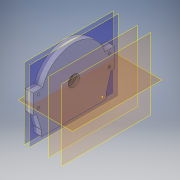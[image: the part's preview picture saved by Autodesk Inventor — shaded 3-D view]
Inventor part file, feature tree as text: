
AUTODESK INVENTOR PART (.ipt)
format: ipt  version: 2019 (Build 230136000, 136)  size: 506,368 bytes
history: native  units: mm
features: sketch x28, extrude x21, mirror x13, plane x12, projected_geometry x11, fillet x4, hole x3, other x2
ambient origin geometry x8: Origin, YZ Plane, XZ Plane, XY Plane, X Axis, Y Axis, Z Axis, Center Point
bodies: Body1 (feature_tree)
feature tree (94):
  other  "實體1"
  extrude  "擠出1"  Depth=123.43mm
  plane  "工作平面2"
  extrude  "擠出3"  Depth=160.0mm
  plane  "工作平面3"
  sketch  "草圖5"
  extrude  "擠出4"  Depth=120.0mm TaperAngle=0.0deg
  extrude  "擠出5"  [1 undecoded]
  plane  "工作平面4"
  extrude  "擠出7"  Depth=130.0mm
  plane  "工作平面5"
  extrude  "擠出9"  Depth=15.0mm TaperAngle=0.0deg
  extrude  "擠出10"  [1 undecoded]
  extrude  "擠出11"  Depth=140.0mm
  extrude  "擠出12"  Depth=10.0mm TaperAngle=0.0deg
  mirror  "鏡射1"
  fillet  "圓角2"  Radius=10.0mm
  fillet  "圓角3"  Radius=10.0mm
  sketch  "草圖16"
  plane  "工作平面7"
  mirror  "鏡射2"
  fillet  "圓角5"  [1 undecoded]
  fillet  "圓角6"  Radius=10.0mm
  plane  "工作平面8"
  plane  "工作平面9"
  sketch  "草圖20"
  sketch  "草圖21"
  extrude  "擠出15"  [1 undecoded]
  plane  "工作平面10"
  extrude  "擠出16"  Depth=10.0mm
  extrude  "擠出17"  Depth=10.0mm TaperAngle=0.0deg
  plane  "工作平面11"
  extrude  "擠出19"  Depth=10.0mm TaperAngle=0.0deg
  extrude  "擠出20"  Depth=160.0mm
  mirror  "鏡射3"
  mirror  "鏡射4"
  extrude  "擠出21"  Depth=80.0mm
  mirror  "鏡射7"
  plane  "工作平面15"
  mirror  "鏡射9"
  hole  "孔2"  [1 undecoded]
  mirror  "鏡射10"
  mirror  "鏡射11"
  hole  "孔3"  [1 undecoded]
  mirror  "鏡射12"
  mirror  "鏡射13"
  extrude  "擠出22"  Depth=160.0mm
  extrude  "擠出23"  Depth=120.0mm TaperAngle=0.0deg
  extrude  "擠出24"  Depth=120.0mm TaperAngle=0.0deg
  extrude  "擠出25"  Depth=25.0mm
  extrude  "擠出27"  Depth=20.0mm
  extrude  "擠出28"  Depth=2.0mm
  mirror  "鏡射14"
  plane  "工作平面17"
  hole  "孔4"  [1 undecoded]
  mirror  "鏡射15"
  mirror  "鏡射16"
  other  "分割1"
  sketch  "草圖1"
  sketch  "草圖4"
  sketch  "草圖6"
  sketch  "草圖7"
  projected_geometry  "投影迴路1"
  sketch  "草圖9"
  projected_geometry  "投影迴路4"
  sketch  "草圖11"
  sketch  "草圖12"
  projected_geometry  "投影迴路6"
  sketch  "草圖13"
  projected_geometry  "投影迴路7"
  sketch  "草圖14"
  plane  "工作平面6"
  sketch  "草圖17"
  projected_geometry  "投影迴路8"
  sketch  "草圖24"
  projected_geometry  "投影迴路11"
  sketch  "草圖25"
  sketch  "草圖26"
  sketch  "草圖27"
  sketch  "草圖28"
  sketch  "草圖29"
  projected_geometry  "投影迴路12"
  sketch  "草圖30"
  sketch  "草圖31"
  sketch  "草圖32"
  projected_geometry  "投影迴路13"
  projected_geometry  "投影迴路14"
  projected_geometry  "投影迴路15"
  sketch  "草圖33"
  sketch  "草圖34"
  sketch  "草圖35"
  projected_geometry  "投影迴路16"
  sketch  "草圖36"
  sketch  "草圖37"
note: 7 required parameter values undecoded (feature->parameter linkage not recoverable at this tier; creation-order binding heuristic only, values carry confidence <= 0.55)
